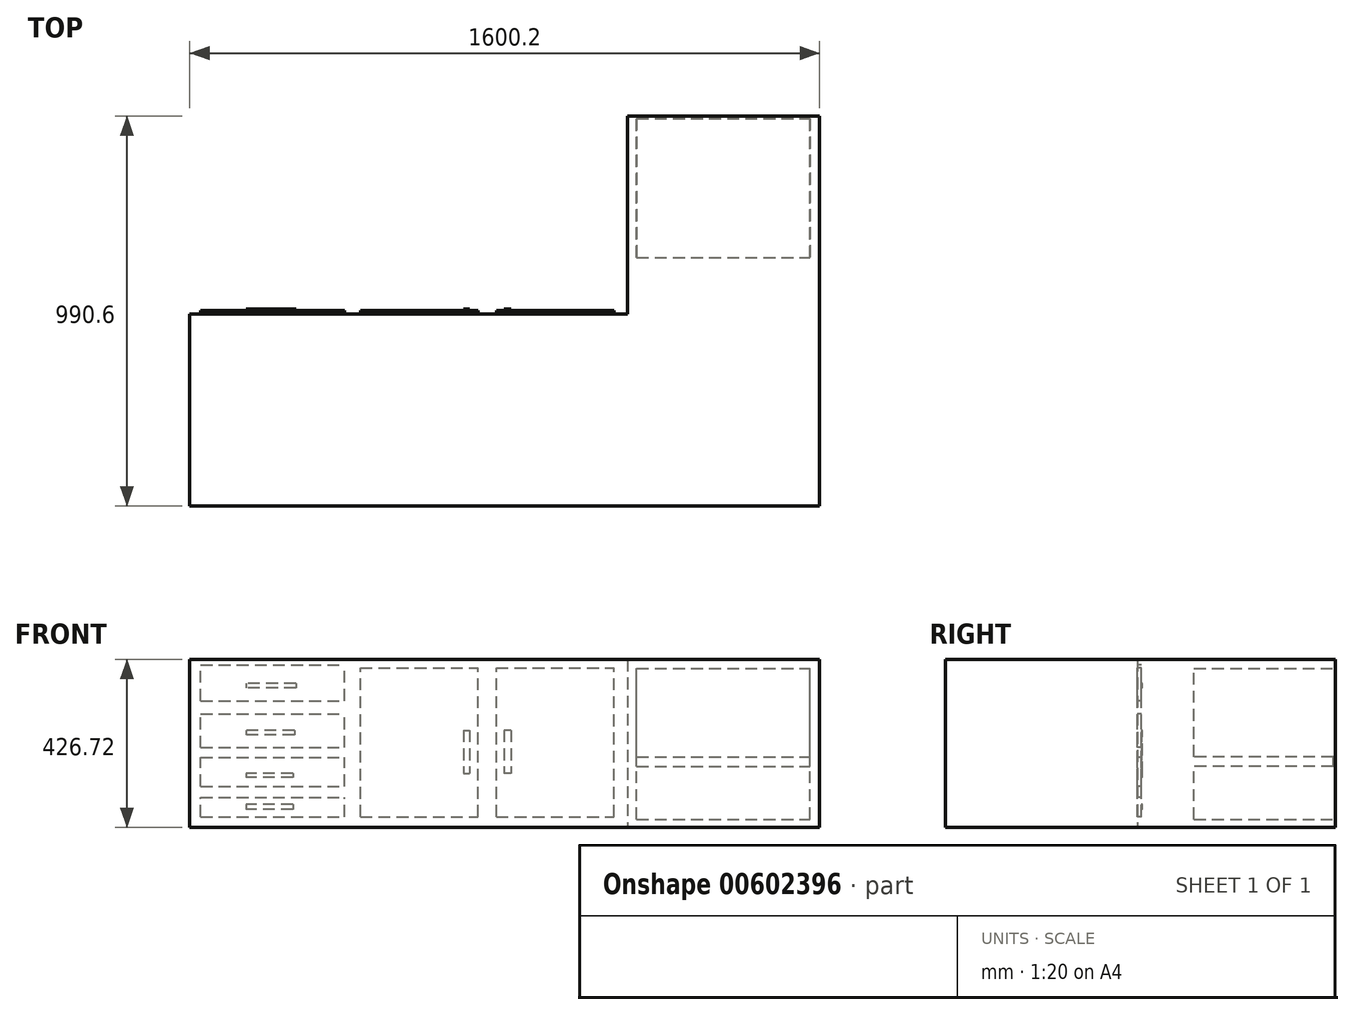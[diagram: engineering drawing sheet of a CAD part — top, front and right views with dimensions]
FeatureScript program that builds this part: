
annotation { "Feature Type Name" : "Feature", "Feature Type Description" : "" }
export const myFeature = defineFeature(function(context is Context, id is Id, definition is map)
    precondition{}
    {
        {
            var Q0;
            Q0=qCreatedBy(makeId("Top.planeOp"),FACE);
            var sketch = newSketch(context, id + "F0", { "sketchPlane" : qUnion([Q0])});
            skLineSegment(sketch, "E0", {"start": v(0, 0) * mm, "end": v(1600.2, 0) * mm});
            skLineSegment(sketch, "E1", {"start": v(1600.2, 0) * mm, "end": v(1600.2, 990.6) * mm});
            skLineSegment(sketch, "E2", {"start": v(1600.2, 990.6) * mm, "end": v(1112.52, 990.6) * mm});
            skLineSegment(sketch, "E3", {"start": v(1112.52, 990.6) * mm, "end": v(1112.52, 487.68) * mm});
            skLineSegment(sketch, "E4", {"start": v(1112.52, 487.68) * mm, "end": v(0, 487.68) * mm});
            skLineSegment(sketch, "E5", {"start": v(0, 487.68) * mm, "end": v(0, 0) * mm});
            skSolve(sketch);
        }
        {
            var Q0;
            Q0=makeQuery(id+"F0.imprint","IMPRINT",FACE,{"disambiguationData":[TD([[makeQuery(id+"F0.imprint","IMPRINT",EDGE,{"derivedFrom":sQuery(id+"F0.wireOp",EDGE,"E0")}),1.0]])]});
            extrude(context, id + "F1", {"entities" : qUnion([Q0]), "depth" : 426.72 * mm, "offsetDistance" : 30.48 * mm});
        }
        {
            var Q0;
            Q0=makeQuery(id+"F1.opExtrude","SWEPT_FACE",FACE,{"disambiguationData":[OSD([sQuery(id+"F0.wireOp",EDGE,"E4")])]});
            var sketch = newSketch(context, id + "F2", { "sketchPlane" : qUnion([Q0])});
            skLineSegment(sketch, "E6.bottom", {"start": v(-27.25, 27.03) * mm, "end": v(-393.01, 27.03) * mm});
            skLineSegment(sketch, "E6.top", {"start": v(-27.25, 75.8) * mm, "end": v(-393.01, 75.8) * mm});
            skLineSegment(sketch, "E6.left", {"start": v(-27.25, 27.03) * mm, "end": v(-27.25, 75.8) * mm});
            skLineSegment(sketch, "E6.right", {"start": v(-393.01, 27.03) * mm, "end": v(-393.01, 75.8) * mm});
            skLineSegment(sketch, "E7.bottom", {"start": v(-27.25, 104.75) * mm, "end": v(-393.01, 104.75) * mm});
            skLineSegment(sketch, "E7.top", {"start": v(-27.25, 177.9) * mm, "end": v(-393.01, 177.9) * mm});
            skLineSegment(sketch, "E7.left", {"start": v(-27.25, 104.75) * mm, "end": v(-27.25, 177.9) * mm});
            skLineSegment(sketch, "E7.right", {"start": v(-393.01, 104.75) * mm, "end": v(-393.01, 177.9) * mm});
            skLineSegment(sketch, "E8.bottom", {"start": v(-27.25, 203.05) * mm, "end": v(-393.01, 203.05) * mm});
            skLineSegment(sketch, "E8.top", {"start": v(-27.25, 288.4) * mm, "end": v(-393.01, 288.4) * mm});
            skLineSegment(sketch, "E8.left", {"start": v(-27.25, 203.05) * mm, "end": v(-27.25, 288.4) * mm});
            skLineSegment(sketch, "E8.right", {"start": v(-393.01, 203.05) * mm, "end": v(-393.01, 288.4) * mm});
            skLineSegment(sketch, "E9.bottom", {"start": v(-27.25, 321.92) * mm, "end": v(-393.01, 321.92) * mm});
            skLineSegment(sketch, "E9.top", {"start": v(-27.25, 413.36) * mm, "end": v(-393.01, 413.36) * mm});
            skLineSegment(sketch, "E9.left", {"start": v(-27.25, 321.92) * mm, "end": v(-27.25, 413.36) * mm});
            skLineSegment(sketch, "E9.right", {"start": v(-393.01, 321.92) * mm, "end": v(-393.01, 413.36) * mm});
            skLineSegment(sketch, "E10.bottom", {"start": v(-433.24, 27.03) * mm, "end": v(-731.94, 27.03) * mm});
            skLineSegment(sketch, "E10.top", {"start": v(-433.24, 404.98) * mm, "end": v(-731.94, 404.98) * mm});
            skLineSegment(sketch, "E10.left", {"start": v(-433.24, 27.03) * mm, "end": v(-433.24, 404.98) * mm});
            skLineSegment(sketch, "E10.right", {"start": v(-731.94, 27.03) * mm, "end": v(-731.94, 404.98) * mm});
            skLineSegment(sketch, "E11.bottom", {"start": v(-779, 27.03) * mm, "end": v(-1077.7, 27.03) * mm});
            skLineSegment(sketch, "E11.top", {"start": v(-779, 404.98) * mm, "end": v(-1077.7, 404.98) * mm});
            skLineSegment(sketch, "E11.left", {"start": v(-779, 27.03) * mm, "end": v(-779, 404.98) * mm});
            skLineSegment(sketch, "E11.right", {"start": v(-1077.7, 27.03) * mm, "end": v(-1077.7, 404.98) * mm});
            skSolve(sketch);
        }
        {
            var Q0;
            Q0=makeQuery(id+"F2.imprint","IMPRINT",FACE,{"disambiguationData":[TD([[makeQuery(id+"F2.imprint","IMPRINT",EDGE,{"derivedFrom":sQuery(id+"F2.wireOp",EDGE,"E6.bottom")}),-1.0]])]});
            var Q1;
            Q1=makeQuery(id+"F2.imprint","IMPRINT",FACE,{"disambiguationData":[TD([[makeQuery(id+"F2.imprint","IMPRINT",EDGE,{"derivedFrom":sQuery(id+"F2.wireOp",EDGE,"E7.bottom")}),-1.0]])]});
            var Q2;
            Q2=makeQuery(id+"F2.imprint","IMPRINT",FACE,{"disambiguationData":[TD([[makeQuery(id+"F2.imprint","IMPRINT",EDGE,{"derivedFrom":sQuery(id+"F2.wireOp",EDGE,"E8.bottom")}),-1.0]])]});
            var Q3;
            Q3=makeQuery(id+"F2.imprint","IMPRINT",FACE,{"disambiguationData":[TD([[makeQuery(id+"F2.imprint","IMPRINT",EDGE,{"derivedFrom":sQuery(id+"F2.wireOp",EDGE,"E9.bottom")}),-1.0]])]});
            var Q4;
            Q4=makeQuery(id+"F2.imprint","IMPRINT",FACE,{"disambiguationData":[TD([[makeQuery(id+"F2.imprint","IMPRINT",EDGE,{"derivedFrom":sQuery(id+"F2.wireOp",EDGE,"E10.bottom")}),-1.0]])]});
            var Q5;
            Q5=makeQuery(id+"F2.imprint","IMPRINT",FACE,{"disambiguationData":[TD([[makeQuery(id+"F2.imprint","IMPRINT",EDGE,{"derivedFrom":sQuery(id+"F2.wireOp",EDGE,"E11.bottom")}),-1.0]])]});
            extrude(context, id + "F3", {"entities" : qUnion([Q0, Q1, Q2, Q3, Q4, Q5]), "operationType" : NewBodyOperationType.ADD, "depth" : 9.14 * mm, "offsetDistance" : 30.48 * mm});
        }
        {
            var Q0;
            Q0=makeQuery(id+"F1.opExtrude","SWEPT_FACE",FACE,{"disambiguationData":[OSD([sQuery(id+"F0.wireOp",EDGE,"E4")])]});
            var sketch = newSketch(context, id + "F4", { "sketchPlane" : qUnion([Q0])});
            skLineSegment(sketch, "E12.bottom", {"start": v(-142.43, 46.1) * mm, "end": v(-261.66, 46.1) * mm});
            skLineSegment(sketch, "E12.top", {"start": v(-142.43, 58.03) * mm, "end": v(-261.66, 58.03) * mm});
            skLineSegment(sketch, "E12.left", {"start": v(-142.43, 46.1) * mm, "end": v(-142.43, 58.03) * mm});
            skLineSegment(sketch, "E12.right", {"start": v(-261.66, 46.1) * mm, "end": v(-261.66, 58.03) * mm});
            skLineSegment(sketch, "E13.bottom", {"start": v(-142.43, 127.58) * mm, "end": v(-261.66, 127.58) * mm});
            skLineSegment(sketch, "E13.top", {"start": v(-142.43, 137.52) * mm, "end": v(-261.66, 137.52) * mm});
            skLineSegment(sketch, "E13.left", {"start": v(-142.43, 127.58) * mm, "end": v(-142.43, 137.52) * mm});
            skLineSegment(sketch, "E13.right", {"start": v(-261.66, 127.58) * mm, "end": v(-261.66, 137.52) * mm});
            skLineSegment(sketch, "E14.bottom", {"start": v(-142.43, 234.9) * mm, "end": v(-265.63, 234.9) * mm});
            skLineSegment(sketch, "E14.top", {"start": v(-142.43, 246.81) * mm, "end": v(-265.63, 246.81) * mm});
            skLineSegment(sketch, "E14.left", {"start": v(-142.43, 234.9) * mm, "end": v(-142.43, 246.81) * mm});
            skLineSegment(sketch, "E14.right", {"start": v(-265.63, 234.9) * mm, "end": v(-265.63, 246.81) * mm});
            skLineSegment(sketch, "E15.bottom", {"start": v(-142.43, 354.12) * mm, "end": v(-269.6, 354.12) * mm});
            skLineSegment(sketch, "E15.top", {"start": v(-142.43, 366.04) * mm, "end": v(-269.6, 366.04) * mm});
            skLineSegment(sketch, "E15.left", {"start": v(-142.43, 354.12) * mm, "end": v(-142.43, 366.04) * mm});
            skLineSegment(sketch, "E15.right", {"start": v(-269.6, 354.12) * mm, "end": v(-269.6, 366.04) * mm});
            skLineSegment(sketch, "E16.bottom", {"start": v(-710.76, 137.52) * mm, "end": v(-694.86, 137.52) * mm});
            skLineSegment(sketch, "E16.top", {"start": v(-710.76, 246.81) * mm, "end": v(-694.86, 246.81) * mm});
            skLineSegment(sketch, "E16.left", {"start": v(-710.76, 137.52) * mm, "end": v(-710.76, 246.81) * mm});
            skLineSegment(sketch, "E16.right", {"start": v(-694.86, 137.52) * mm, "end": v(-694.86, 246.81) * mm});
            skLineSegment(sketch, "E17.bottom", {"start": v(-798.2, 137.52) * mm, "end": v(-816.08, 137.52) * mm});
            skLineSegment(sketch, "E17.top", {"start": v(-798.2, 246.81) * mm, "end": v(-816.08, 246.81) * mm});
            skLineSegment(sketch, "E17.left", {"start": v(-798.2, 137.52) * mm, "end": v(-798.2, 246.81) * mm});
            skLineSegment(sketch, "E17.right", {"start": v(-816.08, 137.52) * mm, "end": v(-816.08, 246.81) * mm});
            skSolve(sketch);
        }
        {
            var Q0;
            Q0 = qSketchRegion(id + "F4", true);
            extrude(context, id + "F5", {"entities" : qUnion([Q0]), "operationType" : NewBodyOperationType.ADD, "depth" : 12.2 * mm, "offsetDistance" : 30.48 * mm});
        }
        {
            var Q0;
            Q0=makeQuery(id+"F1.opExtrude","SWEPT_FACE",FACE,{"disambiguationData":[OSD([sQuery(id+"F0.wireOp",EDGE,"E2")])]});
            var sketch = newSketch(context, id + "F6", { "sketchPlane" : qUnion([Q0])});
            skLineSegment(sketch, "E18.bottom", {"start": v(-1135.4, 20.78) * mm, "end": v(-1574.95, 20.78) * mm});
            skLineSegment(sketch, "E18.top", {"start": v(-1135.4, 403.6) * mm, "end": v(-1574.95, 403.6) * mm});
            skLineSegment(sketch, "E18.left", {"start": v(-1135.4, 20.78) * mm, "end": v(-1135.4, 403.6) * mm});
            skLineSegment(sketch, "E18.right", {"start": v(-1574.95, 20.78) * mm, "end": v(-1574.95, 403.6) * mm});
            skSolve(sketch);
        }
        {
            var Q0;
            Q0=makeQuery(id+"F6.imprint","IMPRINT",FACE,{"disambiguationData":[TD([[makeQuery(id+"F6.imprint","IMPRINT",EDGE,{"derivedFrom":sQuery(id+"F6.wireOp",EDGE,"E18.bottom")}),-1.0]])]});
            extrude(context, id + "F7", {"entities" : qUnion([Q0]), "operationType" : NewBodyOperationType.REMOVE, "oppositeDirection" : true, "depth" : 359.66 * mm, "offsetDistance" : 30.48 * mm});
        }
        {
            var Q0;
            Q0=makeQuery(id+"F7.boolean.opBoolean","COPY",FACE,{"derivedFrom":makeQuery(id+"F7.opExtrude","CAP_FACE",FACE,{"disambiguationData":[OSD([sQuery(id+"F6.wireOp",EDGE,"E18.bottom"),sQuery(id+"F6.wireOp",EDGE,"E18.top"),sQuery(id+"F6.wireOp",EDGE,"E18.left"),sQuery(id+"F6.wireOp",EDGE,"E18.right")])],"isStart":false})});
            var sketch = newSketch(context, id + "F8", { "sketchPlane" : qUnion([Q0])});
            skLineSegment(sketch, "E19.bottom", {"start": v(-1135.4, 155.48) * mm, "end": v(-1574.95, 155.48) * mm});
            skLineSegment(sketch, "E19.top", {"start": v(-1135.4, 179.1) * mm, "end": v(-1574.95, 179.1) * mm});
            skLineSegment(sketch, "E19.left", {"start": v(-1135.4, 155.48) * mm, "end": v(-1135.4, 179.1) * mm});
            skLineSegment(sketch, "E19.right", {"start": v(-1574.95, 155.48) * mm, "end": v(-1574.95, 179.1) * mm});
            skSolve(sketch);
        }
        {
            var Q0;
            Q0=makeQuery(id+"F8.imprint","IMPRINT",FACE,{"disambiguationData":[TD([[makeQuery(id+"F8.imprint","IMPRINT",EDGE,{"derivedFrom":sQuery(id+"F8.wireOp",EDGE,"E19.bottom")}),-1.0]])]});
            extrude(context, id + "F9", {"entities" : qUnion([Q0]), "operationType" : NewBodyOperationType.ADD, "depth" : 353.57 * mm, "offsetDistance" : 30.48 * mm});
        }
    });
